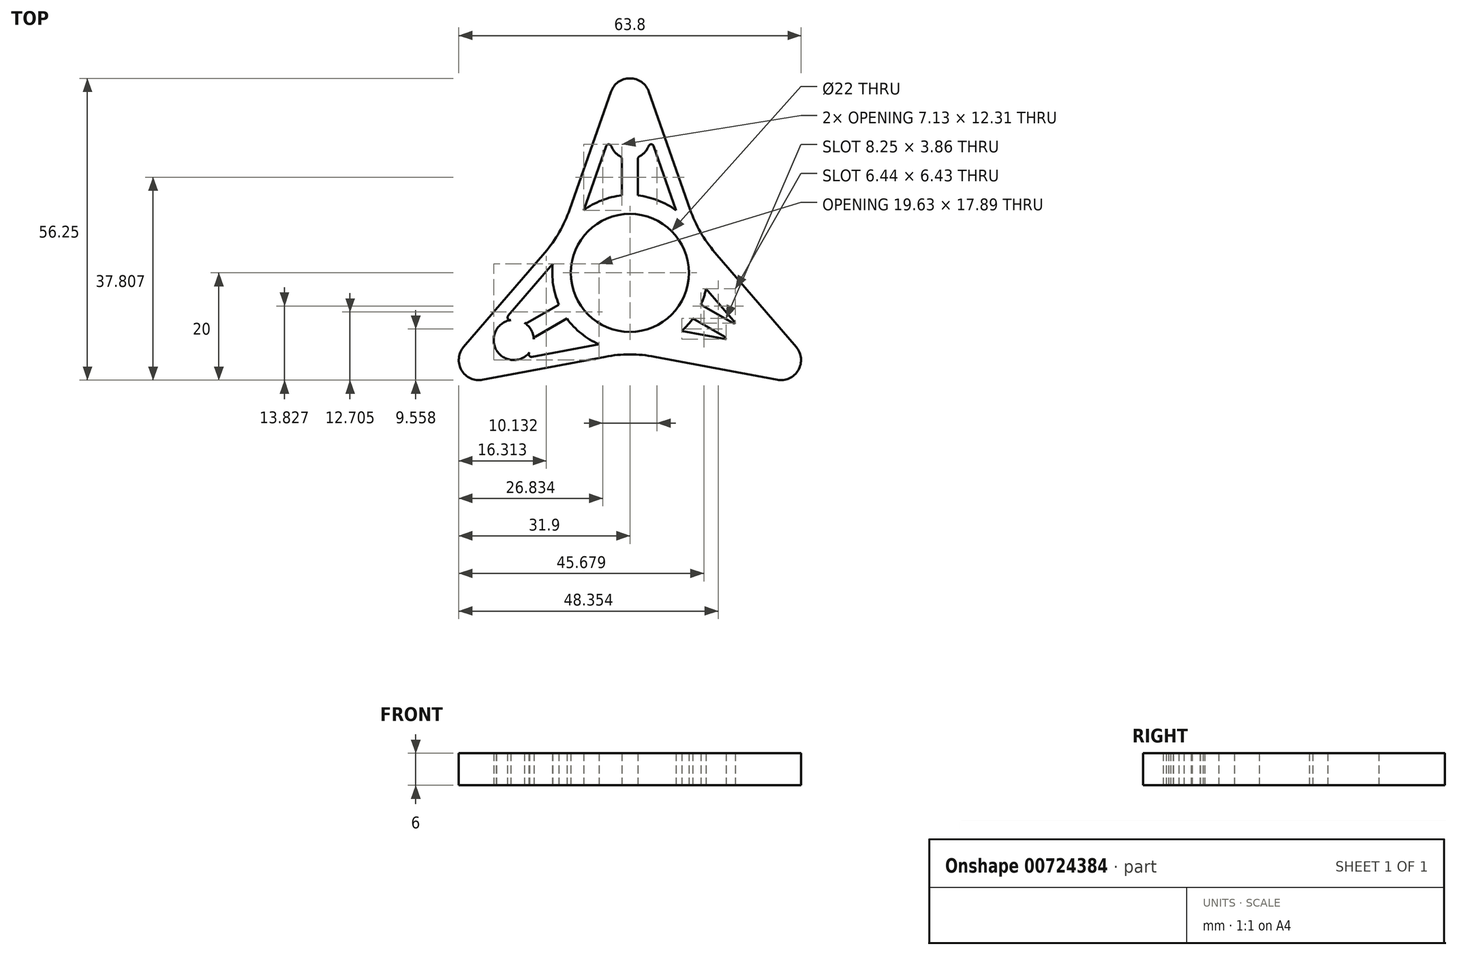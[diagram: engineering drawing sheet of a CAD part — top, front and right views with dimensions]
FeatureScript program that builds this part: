
annotation { "Feature Type Name" : "Feature", "Feature Type Description" : "" }
export const myFeature = defineFeature(function(context is Context, id is Id, definition is map)
    precondition{}
    {
        {
            var Q0;
            Q0=qCreatedBy(makeId("Top.planeOp"),FACE);
            var sketch = newSketch(context, id + "F0", { "sketchPlane" : qUnion([Q0])});
            skCircle(sketch, "E0", {"center": v(0, 0) * mm, "radius": 11 * mm});
            skArc(sketch, "E1", {"start": v(-11.74, -8.51) * mm, "mid": v(-9.08, -11.3) * mm, "end": v(-5.77, -13.3) * mm});
            skLineSegment(sketch, "E2", {"start": v(0, 40.81) * mm, "end": v(0, -43.66) * mm, "construction": true});
            skLineSegment(sketch, "E3", {"start": v(54.3, -31.35) * mm, "end": v(-41.87, 24.17) * mm, "construction": true});
            skLineSegment(sketch, "E4", {"start": v(-54.3, -31.35) * mm, "end": v(45.05, 26.01) * mm, "construction": true});
            skArc(sketch, "E5", {"start": v(3.54, 33.74) * mm, "mid": v(0, 36.25) * mm, "end": v(-3.54, 33.74) * mm});
            skCircle(sketch, "E6.1.0", {"center": v(-28.15, -16.25) * mm, "radius": 3.75 * mm});
            skCircle(sketch, "E6.2.0", {"center": v(28.15, -16.25) * mm, "radius": 3.75 * mm});
            skPoint(sketch, "E7", {"position": v(0, 36.25) * mm});
            skLineSegment(sketch, "E8", {"start": v(3.54, 33.74) * mm, "end": v(11.22, 11.83) * mm});
            skLineSegment(sketch, "E9", {"start": v(4.43, 23.63) * mm, "end": v(8.63, 11.65) * mm});
            skArc(sketch, "E10", {"start": v(-0.06, 28.75) * mm, "mid": v(-3.64, 25.88) * mm, "end": v(-1.76, 21.7) * mm});
            skLineSegment(sketch, "E11.MirrorCS", {"start": v(-4.43, 23.63) * mm, "end": v(-8.63, 11.65) * mm});
            skLineSegment(sketch, "E12.MirrorCS", {"start": v(-3.54, 33.74) * mm, "end": v(-11.22, 11.83) * mm});
            skLineSegment(sketch, "E13.MirrorCS", {"start": v(30.99, -13.8) * mm, "end": v(15.85, 3.8) * mm});
            skLineSegment(sketch, "E14.MirrorCS", {"start": v(22.68, -7.97) * mm, "end": v(14.4, 1.65) * mm});
            skLineSegment(sketch, "E15.MirrorCS", {"start": v(-30.99, -13.8) * mm, "end": v(-15.85, 3.8) * mm});
            skLineSegment(sketch, "E16.MirrorCS", {"start": v(-22.68, -7.97) * mm, "end": v(-14.4, 1.65) * mm});
            skLineSegment(sketch, "E17.MirrorCS", {"start": v(-18.25, -15.65) * mm, "end": v(-5.77, -13.3) * mm});
            skLineSegment(sketch, "E18.MirrorCS", {"start": v(-27.45, -19.93) * mm, "end": v(-4.64, -15.63) * mm});
            skLineSegment(sketch, "E19.MirrorCS", {"start": v(18.25, -15.65) * mm, "end": v(5.77, -13.3) * mm});
            skLineSegment(sketch, "E20.MirrorCS", {"start": v(27.45, -19.93) * mm, "end": v(4.64, -15.63) * mm});
            skArc(sketch, "E21.trimOffspring", {"start": v(-3.5, 23.64) * mm, "mid": v(0, 21.25) * mm, "end": v(3.5, 23.64) * mm});
            skArc(sketch, "E22.trimOffspring", {"start": v(0.06, 28.75) * mm, "mid": v(0, 36.25) * mm, "end": v(-0.06, 28.75) * mm, "construction": true});
            skArc(sketch, "E23.MirrorCS", {"start": v(-24.93, -14.33) * mm, "mid": v(-18.84, -10.02) * mm, "end": v(-23.88, -15.52) * mm});
            skArc(sketch, "E24.MirrorCS", {"start": v(-17.9, -12.37) * mm, "mid": v(-18.1, -13.69) * mm, "end": v(-18.73, -14.85) * mm});
            skArc(sketch, "E25.MirrorCS", {"start": v(24.87, -14.42) * mm, "mid": v(18.1, -11.3) * mm, "end": v(25.38, -12.92) * mm});
            skArc(sketch, "E26.MirrorCS", {"start": v(19.67, -9.32) * mm, "mid": v(20.9, -8.83) * mm, "end": v(22.22, -8.8) * mm});
            skLineSegment(sketch, "E27", {"start": v(-1.5, 21.25) * mm, "end": v(-1.5, 14.42) * mm});
            skLineSegment(sketch, "E28.MirrorCS", {"start": v(1.5, 21.25) * mm, "end": v(1.5, 14.42) * mm});
            skLineSegment(sketch, "E29.MirrorCS", {"start": v(19.15, -9.33) * mm, "end": v(13.24, -5.91) * mm});
            skLineSegment(sketch, "E30.MirrorCS", {"start": v(17.65, -11.92) * mm, "end": v(11.74, -8.51) * mm});
            skLineSegment(sketch, "E31.MirrorCS", {"start": v(-19.15, -9.33) * mm, "end": v(-13.24, -5.91) * mm});
            skLineSegment(sketch, "E32.MirrorCS", {"start": v(-17.65, -11.92) * mm, "end": v(-11.74, -8.51) * mm});
            skArc(sketch, "E33.trimOffspring", {"start": v(-25.38, -12.92) * mm, "mid": v(-23.65, -9.33) * mm, "end": v(-19.67, -9.32) * mm});
            skArc(sketch, "E34.trimOffspring", {"start": v(-25.38, -12.92) * mm, "mid": v(-18.1, -11.3) * mm, "end": v(-24.87, -14.42) * mm});
            skArc(sketch, "E35.trimOffspring", {"start": v(23.88, -15.52) * mm, "mid": v(19.9, -15.82) * mm, "end": v(17.9, -12.37) * mm});
            skArc(sketch, "E36.trimOffspring", {"start": v(13.24, -5.91) * mm, "mid": v(14.33, -2.2) * mm, "end": v(14.4, 1.65) * mm});
            skArc(sketch, "E37.trimOffspring", {"start": v(-1.5, 14.42) * mm, "mid": v(-5.25, 13.52) * mm, "end": v(-8.63, 11.65) * mm});
            skArc(sketch, "E38.trimOffspring", {"start": v(1.76, 21.7) * mm, "mid": v(3.64, 25.88) * mm, "end": v(0.06, 28.75) * mm});
            skArc(sketch, "E39.trimOffspring", {"start": v(-14.4, 1.65) * mm, "mid": v(-14.3, -2.2) * mm, "end": v(-13.24, -5.91) * mm});
            skPoint(sketch, "E40.orphan", {"position": v(-11, 9.45) * mm});
            skPoint(sketch, "E41.orphan", {"position": v(-13.68, 4.8) * mm});
            skArc(sketch, "E42.trimOffspring", {"start": v(5.77, -13.3) * mm, "mid": v(9.08, -11.3) * mm, "end": v(11.74, -8.51) * mm});
            skPoint(sketch, "E43.orphan", {"position": v(2.69, -14.25) * mm});
            skPoint(sketch, "E44.orphan", {"position": v(-2.69, -14.25) * mm});
            skArc(sketch, "E45.trimOffspring", {"start": v(8.63, 11.65) * mm, "mid": v(5.25, 13.5) * mm, "end": v(1.5, 14.42) * mm});
            skPoint(sketch, "E46.orphan", {"position": v(11, 9.45) * mm});
            skPoint(sketch, "E47.orphan", {"position": v(13.68, 4.8) * mm});
            skPoint(sketch, "E48.endSnap0", {"position": v(0.74, 28.68) * mm});
            skPoint(sketch, "E49.center", {"position": v(0.02, 0) * mm});
            skPoint(sketch, "E50.newPointA", {"position": v(-19.43, -15.52) * mm});
            skPoint(sketch, "E50.newPointB", {"position": v(-21.4, -16.25) * mm});
            skArc(sketch, "E50.filletArc", {"start": v(-18.73, -14.85) * mm, "mid": v(-18.77, -15.42) * mm, "end": v(-18.25, -15.65) * mm});
            skPoint(sketch, "E51.newPointA", {"position": v(-24.77, -10.41) * mm});
            skPoint(sketch, "E51.newPointB", {"position": v(-23.15, -9.06) * mm});
            skArc(sketch, "E51.filletArc", {"start": v(-22.68, -7.97) * mm, "mid": v(-22.74, -8.54) * mm, "end": v(-22.22, -8.8) * mm});
            skPoint(sketch, "E52.newPointA", {"position": v(-3.37, 26.66) * mm});
            skPoint(sketch, "E52.newPointB", {"position": v(-3.73, 24.58) * mm});
            skArc(sketch, "E52.filletArc", {"start": v(-3.5, 23.64) * mm, "mid": v(-3.97, 23.96) * mm, "end": v(-4.43, 23.63) * mm});
            skPoint(sketch, "E53.newPointA", {"position": v(3.73, 24.58) * mm});
            skPoint(sketch, "E53.newPointB", {"position": v(3.37, 26.66) * mm});
            skArc(sketch, "E53.filletArc", {"start": v(4.43, 23.63) * mm, "mid": v(3.97, 23.96) * mm, "end": v(3.5, 23.64) * mm});
            skPoint(sketch, "E54.newPointA", {"position": v(24.77, -10.41) * mm});
            skPoint(sketch, "E54.newPointB", {"position": v(23.15, -9.06) * mm});
            skArc(sketch, "E54.filletArc", {"start": v(22.22, -8.8) * mm, "mid": v(22.74, -8.54) * mm, "end": v(22.68, -7.97) * mm});
            skPoint(sketch, "E55.newPointA", {"position": v(21.4, -16.25) * mm});
            skPoint(sketch, "E55.newPointB", {"position": v(19.43, -15.52) * mm});
            skArc(sketch, "E55.filletArc", {"start": v(18.25, -15.65) * mm, "mid": v(18.77, -15.42) * mm, "end": v(18.73, -14.85) * mm});
            skPoint(sketch, "E56.visualSharp", {"position": v(-12.78, 7.38) * mm});
            skArc(sketch, "E56.filletArc", {"start": v(-15.85, 3.8) * mm, "mid": v(-13.16, 7.6) * mm, "end": v(-11.22, 11.83) * mm});
            skPoint(sketch, "E57.visualSharp", {"position": v(12.78, 7.38) * mm});
            skArc(sketch, "E57.filletArc", {"start": v(11.22, 11.83) * mm, "mid": v(13.16, 7.6) * mm, "end": v(15.85, 3.8) * mm});
            skPoint(sketch, "E58.visualSharp", {"position": v(0, -14.76) * mm});
            skArc(sketch, "E58.filletArc", {"start": v(4.64, -15.63) * mm, "mid": v(0, -15.2) * mm, "end": v(-4.64, -15.63) * mm});
            skPoint(sketch, "E59.newPointA", {"position": v(-25.38, -12.92) * mm});
            skPoint(sketch, "E59.newPointB", {"position": v(-24.87, -14.42) * mm});
            skArc(sketch, "E59.filletArc", {"start": v(-19.67, -9.32) * mm, "mid": v(-19.41, -9.4) * mm, "end": v(-19.15, -9.33) * mm});
            skPoint(sketch, "E60.newPointA", {"position": v(-23.88, -15.52) * mm});
            skArc(sketch, "E60.filletArc", {"start": v(-17.65, -11.92) * mm, "mid": v(-17.84, -12.11) * mm, "end": v(-17.9, -12.37) * mm});
            skPoint(sketch, "E61.newPointA", {"position": v(23.88, -15.52) * mm});
            skPoint(sketch, "E61.newPointB", {"position": v(24.93, -14.33) * mm});
            skArc(sketch, "E61.filletArc", {"start": v(17.9, -12.37) * mm, "mid": v(17.84, -12.11) * mm, "end": v(17.65, -11.92) * mm});
            skPoint(sketch, "E62.newPointB", {"position": v(25.38, -12.92) * mm});
            skArc(sketch, "E62.filletArc", {"start": v(19.15, -9.33) * mm, "mid": v(19.41, -9.4) * mm, "end": v(19.67, -9.32) * mm});
            skPoint(sketch, "E63.newPointB", {"position": v(1.5, 28.44) * mm});
            skArc(sketch, "E63.filletArc", {"start": v(1.76, 21.7) * mm, "mid": v(1.57, 21.5) * mm, "end": v(1.5, 21.25) * mm});
            skPoint(sketch, "E64.newPointB", {"position": v(-1.5, 28.44) * mm});
            skArc(sketch, "E64.filletArc", {"start": v(-1.5, 21.25) * mm, "mid": v(-1.57, 21.5) * mm, "end": v(-1.76, 21.7) * mm});
            skLineSegment(sketch, "E65", {"start": v(-1.76, 21.7) * mm, "end": v(-5.48, 11.1) * mm});
            skLineSegment(sketch, "E66.MirrorCS", {"start": v(1.76, 21.7) * mm, "end": v(5.48, 11.1) * mm});
            skLineSegment(sketch, "E67.1.0", {"start": v(-19.67, -9.32) * mm, "end": v(-12.35, -0.8) * mm});
            skLineSegment(sketch, "E67.1.1", {"start": v(-17.9, -12.37) * mm, "end": v(-6.87, -10.3) * mm});
            skLineSegment(sketch, "E67.2.0", {"start": v(17.9, -12.37) * mm, "end": v(6.87, -10.3) * mm});
            skLineSegment(sketch, "E67.2.1", {"start": v(19.67, -9.32) * mm, "end": v(12.35, -0.8) * mm});
            skSolve(sketch);
        }
        {
            var Q0;
            {var subQ6=sQuery(id+"F0.wireOp",EDGE,"E25.MirrorCS");Q0=makeQuery(id+"F0.imprint","IMPRINT",FACE,{"disambiguationData":[TD([[makeQuery(id+"F0.imprint","IMPRINT",EDGE,{"derivedFrom":subQ6}),1.0]])]});}
            var Q1;
            {var subQ0=sQuery(id+"F0.wireOp",EDGE,"E17.MirrorCS");var subQ5=sQuery(id+"F0.wireOp",EDGE,"E24.MirrorCS");var subQ6=makeQuery(id+"F0.imprint","INTERSECT",VERTEX,{"derivedFrom":[subQ0,subQ5]});Q1=makeQuery(id+"F0.imprint","IMPRINT",FACE,{"disambiguationData":[TD([[makeQuery(id+"F0.imprint","IMPRINT",EDGE,{"disambiguationData":[TD([[subQ6,1.0]])],"derivedFrom":subQ5}),-1.0]])]});}
            var Q2;
            {var subQ0=sQuery(id+"F0.wireOp",EDGE,"E16.MirrorCS");var subQ5=sQuery(id+"F0.wireOp",EDGE,"E24.MirrorCS");var subQ6=makeQuery(id+"F0.imprint","INTERSECT",VERTEX,{"derivedFrom":[subQ0,subQ5]});Q2=makeQuery(id+"F0.imprint","IMPRINT",FACE,{"disambiguationData":[TD([[makeQuery(id+"F0.imprint","IMPRINT",EDGE,{"disambiguationData":[TD([[subQ6,-1.0]])],"derivedFrom":subQ5}),-1.0]])]});}
            var Q3;
            {var subQ0=sQuery(id+"F0.wireOp",EDGE,"E23.MirrorCS");Q3=makeQuery(id+"F0.imprint","IMPRINT",FACE,{"disambiguationData":[TD([[makeQuery(id+"F0.imprint","IMPRINT",EDGE,{"derivedFrom":subQ0}),-1.0]])]});}
            var Q4;
            {var subQ0=sQuery(id+"F0.wireOp",EDGE,"E34.trimOffspring");Q4=makeQuery(id+"F0.imprint","IMPRINT",FACE,{"disambiguationData":[TD([[makeQuery(id+"F0.imprint","IMPRINT",EDGE,{"derivedFrom":subQ0}),-1.0]])]});}
            var Q5;
            {var subQ0=sQuery(id+"F0.wireOp",EDGE,"E25.MirrorCS");Q5=makeQuery(id+"F0.imprint","IMPRINT",FACE,{"disambiguationData":[TD([[makeQuery(id+"F0.imprint","IMPRINT",EDGE,{"derivedFrom":subQ0}),-1.0]])]});}
            var Q6;
            {var subQ0=sQuery(id+"F0.wireOp",EDGE,"E10");Q6=makeQuery(id+"F0.imprint","IMPRINT",FACE,{"disambiguationData":[TD([[makeQuery(id+"F0.imprint","IMPRINT",EDGE,{"derivedFrom":subQ0}),1.0]])]});}
            var Q7;
            {var subQ0=sQuery(id+"F0.wireOp",EDGE,"E31.MirrorCS");var subQ1=sQuery(id+"F0.wireOp",EDGE,"E24.MirrorCS");var subQ2=makeQuery(id+"F0.imprint","INTERSECT",VERTEX,{"derivedFrom":[subQ1,subQ0]});Q7=makeQuery(id+"F0.imprint","IMPRINT",FACE,{"disambiguationData":[TD([[makeQuery(id+"F0.imprint","IMPRINT",EDGE,{"disambiguationData":[TD([[subQ2,-1.0]])],"derivedFrom":subQ1}),1.0]])]});}
            var Q8;
            {var subQ0=sQuery(id+"F0.wireOp",EDGE,"E15.MirrorCS");var subQ1=sQuery(id+"F0.wireOp",EDGE,"E12.MirrorCS");var subQ2=makeQuery(id+"F0.imprint","INTERSECT",VERTEX,{"derivedFrom":[subQ1,subQ0]});Q8=makeQuery(id+"F0.imprint","IMPRINT",FACE,{"disambiguationData":[TD([[makeQuery(id+"F0.imprint","IMPRINT",EDGE,{"disambiguationData":[TD([[subQ2,1.0]])],"derivedFrom":subQ1}),-1.0]])]});}
            var Q9;
            {var subQ0=sQuery(id+"F0.wireOp",EDGE,"E13.MirrorCS");var subQ1=sQuery(id+"F0.wireOp",EDGE,"E8");var subQ2=makeQuery(id+"F0.imprint","INTERSECT",VERTEX,{"derivedFrom":[subQ1,subQ0]});Q9=makeQuery(id+"F0.imprint","IMPRINT",FACE,{"disambiguationData":[TD([[makeQuery(id+"F0.imprint","IMPRINT",EDGE,{"disambiguationData":[TD([[subQ2,1.0]])],"derivedFrom":subQ1}),1.0]])]});}
            var Q10;
            {var subQ0=sQuery(id+"F0.wireOp",EDGE,"E20.MirrorCS");var subQ1=sQuery(id+"F0.wireOp",EDGE,"E18.MirrorCS");var subQ2=makeQuery(id+"F0.imprint","INTERSECT",VERTEX,{"derivedFrom":[subQ1,subQ0]});Q10=makeQuery(id+"F0.imprint","IMPRINT",FACE,{"disambiguationData":[TD([[makeQuery(id+"F0.imprint","IMPRINT",EDGE,{"disambiguationData":[TD([[subQ2,1.0]])],"derivedFrom":subQ1}),-1.0]])]});}
            var Q11;
            {var subQ0=sQuery(id+"F0.wireOp",EDGE,"E6.1.0");var subQ1=makeQuery(id+"F0.imprint","INTERSECT",VERTEX,{"derivedFrom":[subQ0,sQuery(id+"F0.wireOp",EDGE,"E15.MirrorCS")]});Q11=makeQuery(id+"F0.imprint","IMPRINT",FACE,{"disambiguationData":[TD([[makeQuery(id+"F0.imprint","IMPRINT",EDGE,{"disambiguationData":[TD([[subQ1,-1.0]])],"derivedFrom":subQ0}),1.0]])]});}
            var Q12;
            {var subQ0=sQuery(id+"F0.wireOp",EDGE,"E6.2.0");var subQ1=makeQuery(id+"F0.imprint","INTERSECT",VERTEX,{"derivedFrom":[subQ0,sQuery(id+"F0.wireOp",EDGE,"E13.MirrorCS")]});Q12=makeQuery(id+"F0.imprint","IMPRINT",FACE,{"disambiguationData":[TD([[makeQuery(id+"F0.imprint","IMPRINT",EDGE,{"disambiguationData":[TD([[subQ1,1.0]])],"derivedFrom":subQ0}),1.0]])]});}
            var Q13;
            Q13=makeQuery(id+"F0.imprint","IMPRINT",FACE,{"disambiguationData":[TD([[makeQuery(id+"F0.imprint","IMPRINT",EDGE,{"derivedFrom":sQuery(id+"F0.wireOp",EDGE,"E0")}),-1.0]])]});
            extrude(context, id + "F1", {"entities" : qUnion([Q0, Q1, Q2, Q3, Q4, Q5, Q6, Q7, Q8, Q9, Q10, Q11, Q12, Q13]), "depth" : 6 * mm, "offsetDistance" : 25 * mm});
        }
    });
